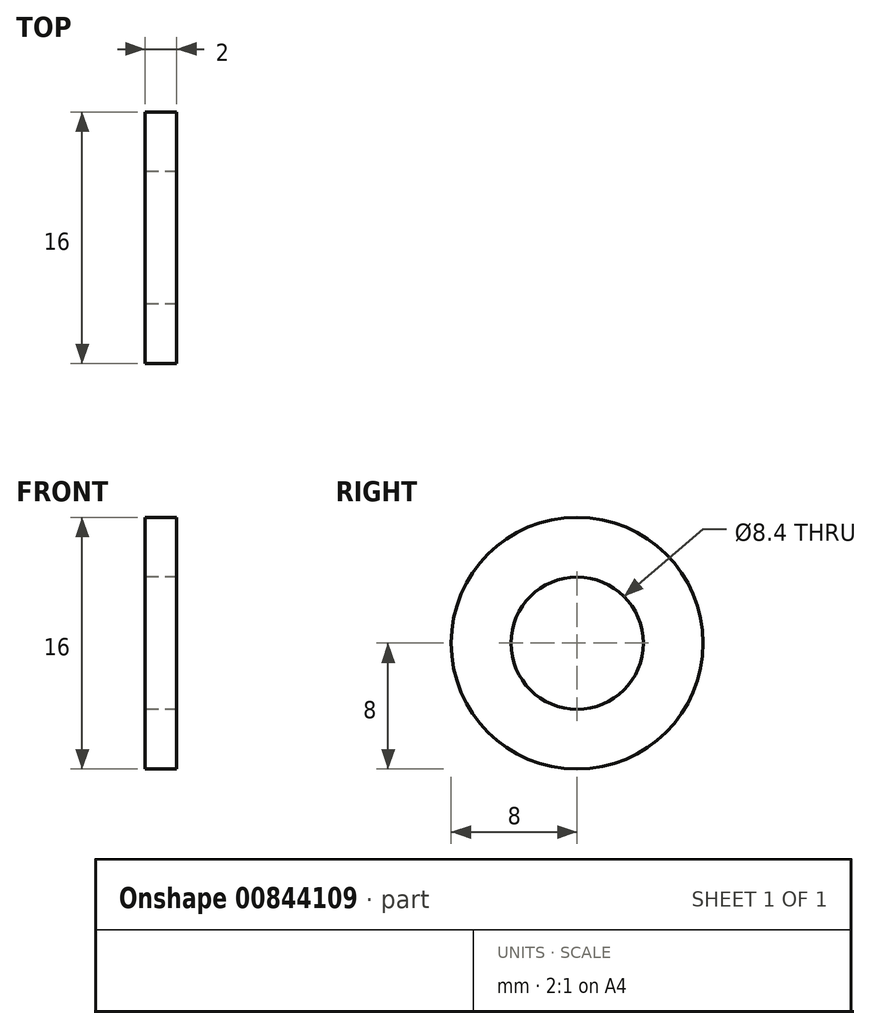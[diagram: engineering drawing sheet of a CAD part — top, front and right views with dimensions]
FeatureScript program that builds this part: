
annotation { "Feature Type Name" : "Feature", "Feature Type Description" : "" }
export const myFeature = defineFeature(function(context is Context, id is Id, definition is map)
    precondition{}
    {
        {
            var Q0;
            Q0=qCreatedBy(makeId("Right.planeOp"),FACE);
            var sketch = newSketch(context, id + "F0", { "sketchPlane" : qUnion([Q0])});
            skCircle(sketch, "E0", {"center": v(0, 0) * mm, "radius": 4.2 * mm});
            skCircle(sketch, "E1", {"center": v(0, 0) * mm, "radius": 8 * mm});
            skSolve(sketch);
        }
        {
            var Q0;
            Q0=makeQuery(id+"F0.imprint","IMPRINT",FACE,{"disambiguationData":[TD([[makeQuery(id+"F0.imprint","IMPRINT",EDGE,{"derivedFrom":sQuery(id+"F0.wireOp",EDGE,"E0")}),-1.0]])]});
            extrude(context, id + "F1", {"entities" : qUnion([Q0]), "endBound" : BoundingType.SYMMETRIC, "depth" : 2 * mm, "offsetDistance" : 25.4 * mm});
        }
    });
